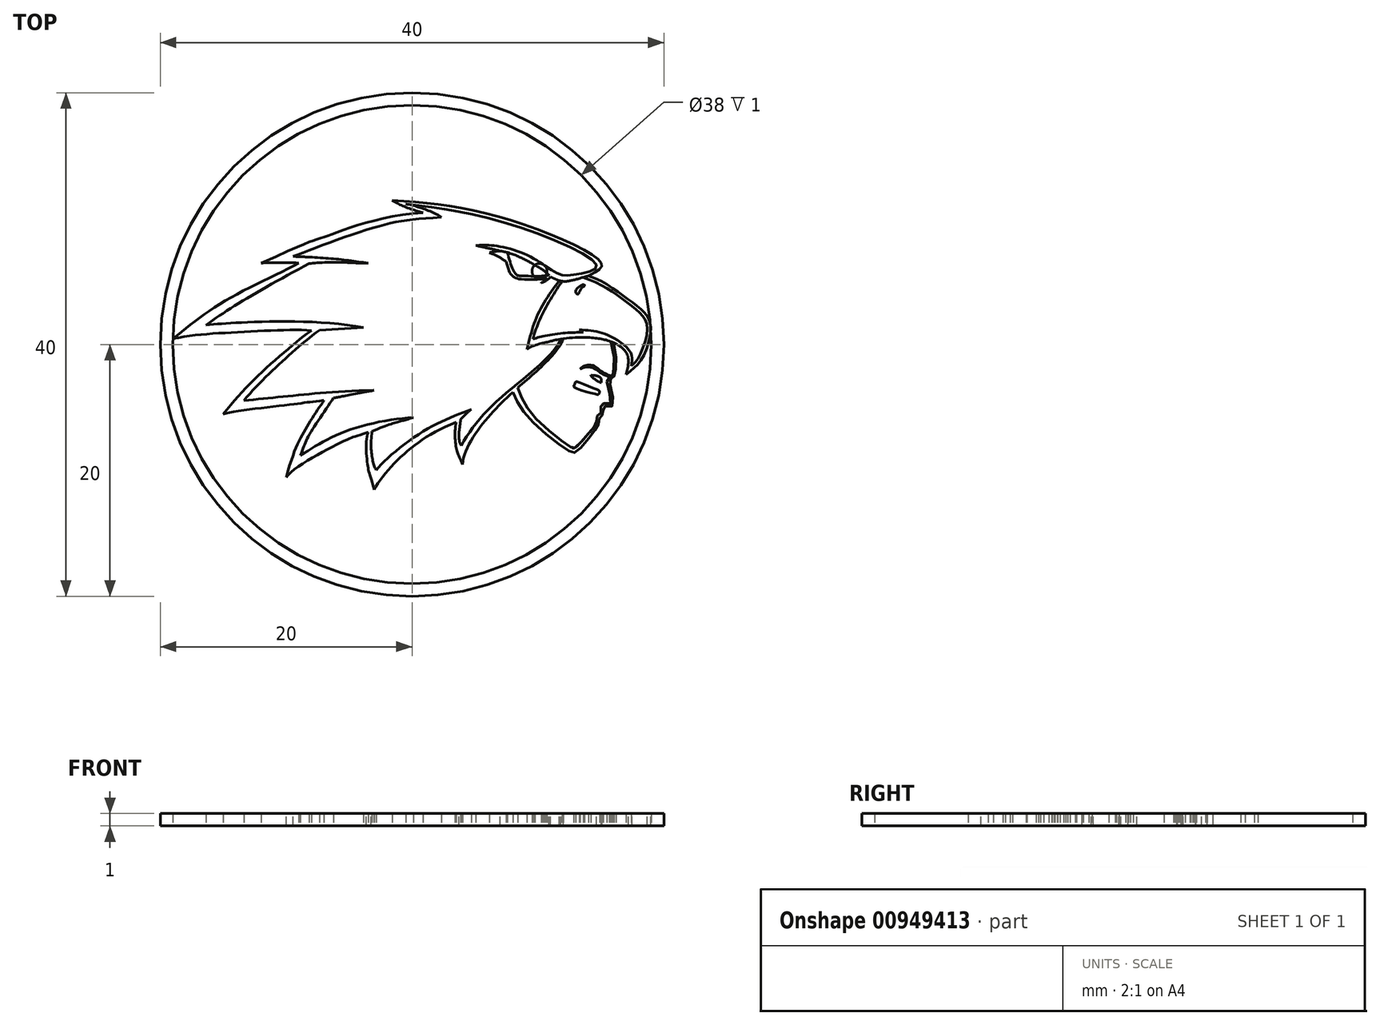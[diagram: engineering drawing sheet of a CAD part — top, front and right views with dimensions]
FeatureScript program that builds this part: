
annotation { "Feature Type Name" : "Feature", "Feature Type Description" : "" }
export const myFeature = defineFeature(function(context is Context, id is Id, definition is map)
    precondition{}
    {
        {
            var Q0;
            Q0=qCreatedBy(makeId("Top.planeOp"),FACE);
            var sketch = newSketch(context, id + "F0", { "sketchPlane" : qUnion([Q0])});
            skCircle(sketch, "E0", {"center": v(0, 0) * mm, "radius": 20 * mm});
            skCircle(sketch, "E1", {"center": v(0, 0) * mm, "radius": 19 * mm});
            skCircle(sketch, "E2", {"center": v(0, 17) * mm, "radius": 2 * mm});
            skSolve(sketch);
        }
        {
            var Q0;
            Q0=makeQuery(id+"F0.imprint","IMPRINT",FACE,{"disambiguationData":[TD([[makeQuery(id+"F0.imprint","IMPRINT",EDGE,{"derivedFrom":sQuery(id+"F0.wireOp",EDGE,"E0")}),1.0]])]});
            extrude(context, id + "F1", {"entities" : qUnion([Q0]), "depth" : 1 * mm, "offsetDistance" : 25 * mm});
        }
        {
            var Q0;
            Q0=qCreatedBy(makeId("Top.planeOp"),FACE);
            var sketch = newSketch(context, id + "F2", { "sketchPlane" : qUnion([Q0])});
            skFitSpline(sketch, "E3", {"points": [v(-1.58, 11.45) * mm, v(7.72, 9.91) * mm, v(15.05, 6.42) * mm, v(14, 5.45) * mm], "startDerivative": vector(21.52, -1.26) * mm, "endDerivative": vector(-13.3, -6.93) * mm});
            skFitSpline(sketch, "E4", {"points": [v(3.5, -6.16) * mm, v(-0.78, -8.83) * mm, v(-3, -11.55) * mm], "startDerivative": vector(-10.76, -4.46) * mm, "endDerivative": vector(-2.73, -5.76) * mm});
            skFitSpline(sketch, "E5", {"points": [v(-3, -11.55) * mm, v(-3.55, -9.5) * mm, v(-3.5, -6.96) * mm], "startDerivative": vector(-2.35, 7.78) * mm, "endDerivative": vector(1.35, 3.27) * mm});
            skFitSpline(sketch, "E6", {"points": [v(-3.5, -6.96) * mm, v(-5.27, -7.6) * mm, v(-10, -10.55) * mm], "startDerivative": vector(-9.15, -3.1) * mm, "endDerivative": vector(-2.97, -4.21) * mm});
            skFitSpline(sketch, "E7", {"points": [v(-10, -10.55) * mm, v(-8.32, -6.48) * mm, v(-7, -4.44) * mm], "startDerivative": vector(3.25, 11.93) * mm, "endDerivative": vector(2.66, 3.7) * mm});
            skFitSpline(sketch, "E8", {"points": [v(-7, -4.44) * mm, v(-9.47, -4.75) * mm, v(-15, -5.55) * mm], "startDerivative": vector(-8.24, -0.84) * mm, "endDerivative": vector(-4.12, -1.43) * mm});
            skFitSpline(sketch, "E9", {"points": [v(-15, -5.55) * mm, v(-11, -1.34) * mm, v(-8, 1.1) * mm], "startDerivative": vector(6.54, 8.64) * mm, "endDerivative": vector(3.53, 2.33) * mm});
            skFitSpline(sketch, "E10", {"points": [v(-8, 1.1) * mm, v(-13.7, 0.98) * mm, v(-19, 0.45) * mm], "startDerivative": vector(-8.4, 0.77) * mm, "endDerivative": vector(-10.04, -2.22) * mm});
            skFitSpline(sketch, "E11", {"points": [v(-19, 0.45) * mm, v(-14.13, 3.88) * mm, v(-8, 7.05) * mm], "startDerivative": vector(8.8, 7.31) * mm, "endDerivative": vector(6.6, 4.65) * mm});
            skFitSpline(sketch, "E12", {"points": [v(-12, 6.45) * mm, v(-6.88, 8.58) * mm, v(0.86, 10.45) * mm], "startDerivative": vector(30.08, 13.67) * mm, "endDerivative": vector(18.85, 0.85) * mm});
            skFitSpline(sketch, "E13", {"points": [v(0.86, 10.45) * mm, v(-0.78, 11.03) * mm, v(-1.58, 11.45) * mm], "startDerivative": vector(-2.07, 0.66) * mm, "endDerivative": vector(-0.97, 0.57) * mm});
            skFitSpline(sketch, "E14", {"points": [v(3.5, -6.16) * mm, v(3.53, -8.34) * mm, v(4, -9.55) * mm], "startDerivative": vector(-0.77, -3.97) * mm, "endDerivative": vector(1.6, -4.4) * mm});
            skFitSpline(sketch, "E15", {"points": [v(4, -9.55) * mm, v(5.91, -5.94) * mm, v(9.09, -2.83) * mm, v(12, 0.45) * mm], "startDerivative": vector(0.54, 10.48) * mm, "endDerivative": vector(2.95, 8.84) * mm});
            skFitSpline(sketch, "E16", {"points": [v(-9, 6.45) * mm, v(-10.52, 6.5) * mm, v(-12, 6.45) * mm], "startDerivative": vector(-3.14, 0.42) * mm, "endDerivative": vector(-2.86, -0.43) * mm});
            skFitSpline(sketch, "E17", {"points": [v(14, 5.45) * mm, v(16.43, 4.12) * mm, v(18.07, 2.88) * mm, v(18.94, 1.52) * mm, v(18.18, -1.26) * mm, v(17, -2.4) * mm], "startDerivative": vector(12.4, -3.48) * mm, "endDerivative": vector(-8.18, -8.07) * mm});
            skFitSpline(sketch, "E18", {"points": [v(17, -2.4) * mm, v(17.07, -0.75) * mm, v(15.73, 0.25) * mm, v(14.63, 0.5) * mm, v(12, 0.45) * mm], "startDerivative": vector(1.76, 6.26) * mm, "endDerivative": vector(-11.27, -1.86) * mm});
            skFitSpline(sketch, "E19", {"points": [v(11, 5.38) * mm, v(9.78, 6.3) * mm, v(7, 7.43) * mm], "startDerivative": vector(-2.8, 3.17) * mm, "endDerivative": vector(-5.7, 0.83) * mm});
            skFitSpline(sketch, "E20", {"points": [v(7, 7.43) * mm, v(7.74, 5.78) * mm, v(8, 5.43) * mm, v(8.44, 5.22) * mm, v(10.45, 5.2) * mm, v(10.9, 5.29) * mm, v(11, 5.38) * mm], "startDerivative": vector(6.03, -7.57) * mm, "endDerivative": vector(2.14, 2.82) * mm});
            skCircle(sketch, "E21", {"center": v(10.12, 5.84) * mm, "radius": 0.6 * mm});
            skFitSpline(sketch, "E22", {"points": [v(8, -3.8) * mm, v(9.3, -5.87) * mm, v(12.45, -8.44) * mm, v(13, -8.55) * mm, v(14.33, -7.05) * mm, v(14.82, -6.23) * mm, v(14.93, -5.76) * mm, v(15.19, -5.5) * mm, v(15.2, -4.92) * mm, v(15.93, -4.86) * mm, v(15.7, -2.86) * mm, v(15.92, -2.64) * mm, v(16.1, -2.38) * mm, v(16, 0.14) * mm], "startDerivative": vector(7.5, -17.46) * mm, "endDerivative": vector(-8.07, 26.27) * mm});
            skFitSpline(sketch, "E23", {"points": [v(15.02, -3.03) * mm, v(14.56, -2.8) * mm, v(14.2, -2.44) * mm], "startDerivative": vector(-1.12, 0.33) * mm, "endDerivative": vector(-0.33, 0.79) * mm});
            skFitSpline(sketch, "E24", {"points": [v(14.2, -2.44) * mm, v(14.57, -2.47) * mm, v(14.94, -2.61) * mm, v(15.04, -2.8) * mm, v(15.02, -3.03) * mm], "startDerivative": vector(1.37, -0.38) * mm, "endDerivative": vector(-0.15, -0.97) * mm});
            skFitSpline(sketch, "E25", {"points": [v(15.68, -2.55) * mm, v(15.48, -2.5) * mm, v(14.93, -2.22) * mm, v(14.67, -2.02) * mm, v(14.03, -1.79) * mm, v(13.34, -1.95) * mm], "startDerivative": vector(-2.24, 0.34) * mm, "endDerivative": vector(-2.61, -1.2) * mm});
            skFitSpline(sketch, "E26", {"points": [v(13.34, -1.95) * mm, v(13.86, -1.65) * mm, v(14.3, -1.65) * mm, v(14.57, -1.77) * mm, v(15.07, -2.15) * mm, v(15.55, -2.4) * mm, v(15.89, -2.49) * mm], "startDerivative": vector(2.26, 2.4) * mm, "endDerivative": vector(2.1, 0.6) * mm});
            skFitSpline(sketch, "E27", {"points": [v(15.68, -2.55) * mm, v(15.8, -2.54) * mm, v(15.89, -2.49) * mm], "startDerivative": vector(0.25, -0.06) * mm, "endDerivative": vector(0.25, 0.3) * mm});
            skFitSpline(sketch, "E28", {"points": [v(14.52, -3.93) * mm, v(12.97, -3.46) * mm, v(12.85, -3.33) * mm, v(12.9, -3.2) * mm, v(12.98, -3) * mm, v(13.07, -2.94) * mm, v(13.22, -3) * mm, v(14.68, -3.57) * mm, v(14.86, -3.66) * mm, v(14.9, -3.76) * mm, v(14.84, -3.93) * mm, v(14.78, -3.97) * mm, v(14.52, -3.93) * mm]});
            skFitSpline(sketch, "E29", {"points": [v(12, 0.45) * mm, v(10.73, 0.2) * mm, v(9.12, -0.4) * mm], "startDerivative": vector(-4.79, -0.65) * mm, "endDerivative": vector(-1.75, -1.76) * mm});
            skFitSpline(sketch, "E30", {"points": [v(9.12, -0.4) * mm, v(10.04, 2.5) * mm, v(11.7, 5.07) * mm], "startDerivative": vector(1.47, 5.98) * mm, "endDerivative": vector(3.7, 4.95) * mm});
            skFitSpline(sketch, "E31", {"points": [v(14, 5.45) * mm, v(12.41, 5.04) * mm, v(11.7, 5.07) * mm, v(11, 5.38) * mm], "startDerivative": vector(-4.1, -1.19) * mm, "endDerivative": vector(-2.43, 1.23) * mm});
            skFitSpline(sketch, "E32", {"points": [v(7, 7.43) * mm, v(5.97, 7.67) * mm, v(5.07, 7.87) * mm], "startDerivative": vector(-2.03, 0.53) * mm, "endDerivative": vector(-1.84, 0.4) * mm});
            skFitSpline(sketch, "E33", {"points": [v(5.07, 7.87) * mm, v(6.4, 7.87) * mm, v(9.35, 7) * mm, v(11.6, 5.62) * mm, v(12.86, 5.54) * mm, v(14.66, 6.18) * mm, v(7.76, 9.56) * mm, v(-0.49, 11.17) * mm], "startDerivative": vector(13.05, 0.9) * mm, "endDerivative": vector(-32.62, 3.92) * mm});
            skFitSpline(sketch, "E34", {"points": [v(-0.49, 11.17) * mm, v(0.93, 10.77) * mm, v(2.33, 10.11) * mm], "startDerivative": vector(2.94, -0.6) * mm, "endDerivative": vector(1.78, -1.4) * mm});
            skFitSpline(sketch, "E35", {"points": [v(2.33, 10.11) * mm, v(-3.07, 9.27) * mm, v(-9.44, 7) * mm], "startDerivative": vector(-15.85, -1) * mm, "endDerivative": vector(-7.4, -3.02) * mm});
            skFitSpline(sketch, "E36", {"points": [v(-9.44, 7) * mm, v(-6.18, 6.8) * mm, v(-3.48, 6.45) * mm], "startDerivative": vector(6.38, -0.27) * mm, "endDerivative": vector(5.53, -0.87) * mm});
            skFitSpline(sketch, "E37", {"points": [v(-3.48, 6.45) * mm, v(-6.21, 6.54) * mm, v(-8.18, 6.43) * mm], "startDerivative": vector(-6.33, 0.08) * mm, "endDerivative": vector(-3.05, -0.33) * mm});
            skFitSpline(sketch, "E38", {"points": [v(-8.18, 6.43) * mm, v(-13.5, 3.44) * mm, v(-16.37, 1.55) * mm], "startDerivative": vector(-9.86, -5.27) * mm, "endDerivative": vector(-6.1, -4.23) * mm});
            skFitSpline(sketch, "E39", {"points": [v(-16.37, 1.55) * mm, v(-13.5, 1.75) * mm, v(-3.85, 1.35) * mm], "startDerivative": vector(6.8, 0.6) * mm, "endDerivative": vector(14.41, -2.83) * mm});
            skFitSpline(sketch, "E40", {"points": [v(-3.85, 1.35) * mm, v(-7.35, 1.14) * mm], "startDerivative": vector(-3.5, -0.2) * mm, "endDerivative": vector(-3.5, -0.2) * mm});
            skFitSpline(sketch, "E41", {"points": [v(-7.35, 1.14) * mm, v(-10.41, -1.43) * mm, v(-13.36, -4.46) * mm], "startDerivative": vector(-6.68, -4.88) * mm, "endDerivative": vector(-5.36, -6.32) * mm});
            skFitSpline(sketch, "E42", {"points": [v(-13.36, -4.46) * mm, v(-9.36, -4.06) * mm, v(-3.02, -3.64) * mm], "startDerivative": vector(8.78, 0.94) * mm, "endDerivative": vector(14.42, 0.16) * mm});
            skFitSpline(sketch, "E43", {"points": [v(-3.02, -3.64) * mm, v(-5.54, -4.12) * mm, v(-6.24, -4.25) * mm], "startDerivative": vector(-4.48, -0.91) * mm, "endDerivative": vector(-1.64, -0.24) * mm});
            skFitSpline(sketch, "E44", {"points": [v(-6.24, -4.25) * mm, v(-8.21, -7.25) * mm, v(-8.87, -8.8) * mm], "startDerivative": vector(-3.02, -4.33) * mm, "endDerivative": vector(-1.83, -4.96) * mm});
            skFitSpline(sketch, "E45", {"points": [v(-8.87, -8.8) * mm, v(-5.6, -7.02) * mm, v(0.1, -5.81) * mm], "startDerivative": vector(6.74, 4.12) * mm, "endDerivative": vector(9.55, 0.33) * mm});
            skFitSpline(sketch, "E46", {"points": [v(0.1, -5.81) * mm, v(-1.02, -6.13) * mm, v(-3.18, -6.9) * mm], "startDerivative": vector(-4.07, -1.11) * mm, "endDerivative": vector(-5.58, -2.4) * mm});
            skFitSpline(sketch, "E47", {"points": [v(-3.18, -6.9) * mm, v(-3.14, -9.14) * mm, v(-2.84, -9.97) * mm], "startDerivative": vector(-0.7, -4.41) * mm, "endDerivative": vector(1.32, -1.52) * mm});
            skFitSpline(sketch, "E48", {"points": [v(-2.84, -9.97) * mm, v(0.78, -6.97) * mm, v(4.7, -5.14) * mm], "startDerivative": vector(3.54, 4.6) * mm, "endDerivative": vector(7.5, 2.99) * mm});
            skFitSpline(sketch, "E49", {"points": [v(4.7, -5.14) * mm, v(3.85, -5.96) * mm], "startDerivative": vector(-1.54, -1.24) * mm, "endDerivative": vector(-0.85, -0.81) * mm});
            skFitSpline(sketch, "E50", {"points": [v(3.85, -5.96) * mm, v(3.74, -7.58) * mm, v(3.91, -8.04) * mm], "startDerivative": vector(-0.38, -2.91) * mm, "endDerivative": vector(0.59, -1.08) * mm});
            skFitSpline(sketch, "E51", {"points": [v(3.91, -8.04) * mm, v(5.56, -5.69) * mm, v(8.66, -2.88) * mm, v(11.8, 0.43) * mm], "startDerivative": vector(4.66, 8.5) * mm, "endDerivative": vector(3.92, 9.27) * mm});
            skFitSpline(sketch, "E52", {"points": [v(11.8, 0.43) * mm, v(12, 0.45) * mm], "startDerivative": vector(0.2, 0.03) * mm, "endDerivative": vector(0.2, 0.03) * mm});
            skFitSpline(sketch, "E53", {"points": [v(11.92, 5.03) * mm, v(10.4, 2.5) * mm, v(9.6, 0.43) * mm], "startDerivative": vector(-3.21, -4.76) * mm, "endDerivative": vector(-1.06, -4.44) * mm});
            skFitSpline(sketch, "E54", {"points": [v(9.6, 0.43) * mm, v(10.45, 0.67) * mm, v(12.21, 0.92) * mm, v(13.6, 0.96) * mm], "startDerivative": vector(2.74, 0.91) * mm, "endDerivative": vector(3.8, 0) * mm});
            skFitSpline(sketch, "E55", {"points": [v(13.6, 0.96) * mm, v(13.29, 1.17) * mm], "startDerivative": vector(-0.45, 0.21) * mm, "endDerivative": vector(-0.45, 0.21) * mm});
            skFitSpline(sketch, "E56", {"points": [v(13.29, 1.17) * mm, v(14.52, 1.05) * mm, v(15.83, 0.62) * mm, v(17.37, -0.67) * mm, v(17.4, -1.7) * mm], "startDerivative": vector(5.3, -0.38) * mm, "endDerivative": vector(-0.98, -4.8) * mm});
            skFitSpline(sketch, "E57", {"points": [v(17.4, -1.7) * mm, v(17.94, -1.12) * mm, v(18.7, 1.36) * mm, v(18, 2.6) * mm, v(16.13, 4.03) * mm, v(13.6, 5.34) * mm], "startDerivative": vector(3.88, 3.06) * mm, "endDerivative": vector(-12.32, 4.18) * mm});
            skFitSpline(sketch, "E58", {"points": [v(7.57, 7.3) * mm, v(8.08, 5.8) * mm, v(8.4, 5.5) * mm, v(8.78, 5.45) * mm, v(10.88, 5.51) * mm], "startDerivative": vector(1.53, -5.22) * mm, "endDerivative": vector(2.76, 1.11) * mm});
            skFitSpline(sketch, "E59", {"points": [v(7.48, 6.59) * mm, v(6.84, 6.98) * mm, v(6.14, 7.3) * mm], "startDerivative": vector(-1.21, 0.84) * mm, "endDerivative": vector(-1.25, 0.39) * mm});
            skFitSpline(sketch, "E60", {"points": [v(7, 7.43) * mm, v(6.54, 7.38) * mm, v(6.14, 7.3) * mm], "startDerivative": vector(-0.92, 0.03) * mm, "endDerivative": vector(-1.04, -0.3) * mm});
            skFitSpline(sketch, "E61", {"points": [v(11, 5.38) * mm, v(10.6, 5.04) * mm, v(10.25, 4.9) * mm], "startDerivative": vector(-0.74, -0.71) * mm, "endDerivative": vector(-0.76, -0.25) * mm});
            skFitSpline(sketch, "E62", {"points": [v(10.25, 4.9) * mm, v(10.65, 5.17) * mm, v(10.88, 5.51) * mm], "startDerivative": vector(0.83, 0.5) * mm, "endDerivative": vector(0.41, 0.76) * mm});
            skFitSpline(sketch, "E63", {"points": [v(13.68, 4.76) * mm, v(13.18, 4.53) * mm, v(13.02, 4.13) * mm, v(13.16, 4) * mm, v(13.46, 4.47) * mm, v(13.69, 4.66) * mm, v(13.68, 4.76) * mm]});
            skFitSpline(sketch, "E64", {"points": [v(15.8, 0.23) * mm, v(15.96, -2.32) * mm, v(15.87, -2.55) * mm, v(15.5, -2.74) * mm, v(15.75, -4.67) * mm, v(15.05, -4.7) * mm, v(15, -5.4) * mm, v(14.74, -5.63) * mm, v(14.63, -6.18) * mm, v(14.19, -6.88) * mm, v(12.96, -8.19) * mm, v(12.6, -8.15) * mm, v(9.58, -5.6) * mm, v(8.38, -3.45) * mm], "startDerivative": vector(10.2, -30.63) * mm, "endDerivative": vector(-7.66, 17.6) * mm});
            skFitSpline(sketch, "E65", {"points": [v(10.7, 5.68) * mm, v(10.67, 6.08) * mm, v(10.45, 6.34) * mm], "startDerivative": vector(0.04, 0.82) * mm, "endDerivative": vector(-0.55, 0.49) * mm});
            skFitSpline(sketch, "E66", {"points": [v(3.5, -6.16) * mm, v(3.85, -5.96) * mm], "startDerivative": vector(0.35, 0.2) * mm, "endDerivative": vector(0.35, 0.2) * mm});
            skFitSpline(sketch, "E67", {"points": [v(-2.84, -9.97) * mm, v(-3, -11.55) * mm], "startDerivative": vector(-0.16, -1.59) * mm, "endDerivative": vector(-0.16, -1.59) * mm});
            skFitSpline(sketch, "E68", {"points": [v(-3.18, -6.9) * mm, v(-3.5, -6.96) * mm], "startDerivative": vector(-0.31, -0.06) * mm, "endDerivative": vector(-0.31, -0.06) * mm});
            skFitSpline(sketch, "E69", {"points": [v(-8.87, -8.8) * mm, v(-10, -10.55) * mm], "startDerivative": vector(-1.13, -1.75) * mm, "endDerivative": vector(-1.13, -1.75) * mm});
            skFitSpline(sketch, "E70", {"points": [v(-7, -4.44) * mm, v(-6.24, -4.25) * mm], "startDerivative": vector(0.76, 0.19) * mm, "endDerivative": vector(0.76, 0.19) * mm});
            skFitSpline(sketch, "E71", {"points": [v(-13.36, -4.46) * mm, v(-15, -5.55) * mm], "startDerivative": vector(-1.63, -1.1) * mm, "endDerivative": vector(-1.63, -1.1) * mm});
            skFitSpline(sketch, "E72", {"points": [v(-8, 1.1) * mm, v(-7.35, 1.14) * mm], "startDerivative": vector(0.65, 0.03) * mm, "endDerivative": vector(0.65, 0.03) * mm});
            skFitSpline(sketch, "E73", {"points": [v(-16.37, 1.55) * mm, v(-19, 0.45) * mm], "startDerivative": vector(-2.63, -1.1) * mm, "endDerivative": vector(-2.63, -1.1) * mm});
            skFitSpline(sketch, "E74", {"points": [v(-9, 6.45) * mm, v(-8.18, 6.43) * mm], "startDerivative": vector(0.82, -0.01) * mm, "endDerivative": vector(0.82, -0.01) * mm});
            skFitSpline(sketch, "E75", {"points": [v(-9.44, 7) * mm, v(-12, 6.45) * mm], "startDerivative": vector(-2.56, -0.56) * mm, "endDerivative": vector(-2.56, -0.56) * mm});
            skFitSpline(sketch, "E76", {"points": [v(0.86, 10.45) * mm, v(2.33, 10.11) * mm], "startDerivative": vector(1.48, -0.33) * mm, "endDerivative": vector(1.48, -0.33) * mm});
            skFitSpline(sketch, "E77", {"points": [v(-0.49, 11.17) * mm, v(-1.58, 11.45) * mm], "startDerivative": vector(-1.1, 0.27) * mm, "endDerivative": vector(-1.1, 0.27) * mm});
            skFitSpline(sketch, "E78", {"points": [v(13.6, 5.34) * mm, v(14, 5.45) * mm], "startDerivative": vector(0.4, 0.12) * mm, "endDerivative": vector(0.4, 0.12) * mm});
            skFitSpline(sketch, "E79", {"points": [v(7, 7.43) * mm, v(7.57, 7.3) * mm], "startDerivative": vector(0.57, -0.12) * mm, "endDerivative": vector(0.57, -0.12) * mm});
            skSolve(sketch);
        }
        {
            var Q0;
            {var subQ2=sQuery(id+"F2.wireOp",EDGE,"E59");Q0=makeQuery(id+"F2.imprint","IMPRINT",FACE,{"disambiguationData":[TD([[makeQuery(id+"F2.imprint","IMPRINT",EDGE,{"derivedFrom":subQ2}),-1.0]])]});}
            var Q1;
            Q1=makeQuery(id+"F2.imprint","IMPRINT",FACE,{"disambiguationData":[TD([[makeQuery(id+"F2.imprint","IMPRINT",EDGE,{"derivedFrom":sQuery(id+"F2.wireOp",EDGE,"E63")}),1.0]])]});
            var Q2;
            {var subQ0=sQuery(id+"F2.wireOp",EDGE,"E32");Q2=makeQuery(id+"F2.imprint","IMPRINT",FACE,{"disambiguationData":[TD([[makeQuery(id+"F2.imprint","IMPRINT",EDGE,{"derivedFrom":subQ0}),-1.0]])]});}
            var Q3;
            {var subQ0=sQuery(id+"F2.wireOp",EDGE,"E79");Q3=makeQuery(id+"F2.imprint","IMPRINT",FACE,{"disambiguationData":[TD([[makeQuery(id+"F2.imprint","IMPRINT",EDGE,{"derivedFrom":subQ0}),-1.0]])]});}
            var Q4;
            Q4=makeQuery(id+"F2.imprint","IMPRINT",FACE,{"disambiguationData":[TD([[makeQuery(id+"F2.imprint","IMPRINT",EDGE,{"derivedFrom":sQuery(id+"F2.wireOp",EDGE,"E3")}),-1.0]])]});
            var Q5;
            {var subQ0=sQuery(id+"F2.wireOp",EDGE,"E62");var subQ1=sQuery(id+"F2.wireOp",EDGE,"E20");var subQ2=makeQuery(id+"F2.imprint","INTERSECT",VERTEX,{"derivedFrom":[subQ1,subQ0]});Q5=makeQuery(id+"F2.imprint","IMPRINT",FACE,{"disambiguationData":[TD([[makeQuery(id+"F2.imprint","IMPRINT",EDGE,{"disambiguationData":[TD([[subQ2,-1.0]])],"derivedFrom":subQ1}),-1.0]])]});}
            var Q6;
            {var subQ1=sQuery(id+"F2.wireOp",EDGE,"E20");var subQ4=sQuery(id+"F2.wireOp",EDGE,"E62");var subQ6=makeQuery(id+"F2.imprint","INTERSECT",VERTEX,{"derivedFrom":[subQ1,subQ4]});Q6=makeQuery(id+"F2.imprint","IMPRINT",FACE,{"disambiguationData":[TD([[makeQuery(id+"F2.imprint","IMPRINT",EDGE,{"disambiguationData":[TD([[subQ6,-1.0]])],"derivedFrom":subQ1}),1.0]])]});}
            var Q7;
            {var subQ0=sQuery(id+"F2.wireOp",EDGE,"E21");var subQ1=sQuery(id+"F2.wireOp",EDGE,"E19");var subQ3=makeQuery(id+"F2.imprint","INTERSECT",VERTEX,{"derivedFrom":[subQ1,subQ0]});Q7=makeQuery(id+"F2.imprint","IMPRINT",FACE,{"disambiguationData":[TD([[makeQuery(id+"F2.imprint","IMPRINT",EDGE,{"disambiguationData":[TD([[subQ3,-1.0]])],"derivedFrom":subQ0}),1.0]])]});}
            var Q8;
            {var subQ4=sQuery(id+"F2.wireOp",EDGE,"E14");Q8=makeQuery(id+"F2.imprint","IMPRINT",FACE,{"disambiguationData":[TD([[makeQuery(id+"F2.imprint","IMPRINT",EDGE,{"derivedFrom":subQ4}),1.0]])]});}
            var Q9;
            {var subQ0=sQuery(id+"F2.wireOp",EDGE,"E22");Q9=makeQuery(id+"F2.imprint","IMPRINT",FACE,{"disambiguationData":[TD([[makeQuery(id+"F2.imprint","IMPRINT",EDGE,{"derivedFrom":subQ0}),1.0]])]});}
            var Q10;
            Q10=makeQuery(id+"F2.imprint","IMPRINT",FACE,{"disambiguationData":[TD([[makeQuery(id+"F2.imprint","IMPRINT",EDGE,{"derivedFrom":sQuery(id+"F2.wireOp",EDGE,"E23")}),-1.0]])]});
            var Q11;
            Q11=makeQuery(id+"F2.imprint","IMPRINT",FACE,{"disambiguationData":[TD([[makeQuery(id+"F2.imprint","IMPRINT",EDGE,{"derivedFrom":sQuery(id+"F2.wireOp",EDGE,"E28")}),-1.0]])]});
            var Q12;
            Q12=makeQuery(id+"F2.imprint","IMPRINT",FACE,{"disambiguationData":[TD([[makeQuery(id+"F2.imprint","IMPRINT",EDGE,{"derivedFrom":sQuery(id+"F2.wireOp",EDGE,"E25")}),-1.0]])]});
            var Q13;
            Q13=makeQuery(id+"F2.imprint","IMPRINT",FACE,{"disambiguationData":[TD([[makeQuery(id+"F2.imprint","IMPRINT",EDGE,{"derivedFrom":sQuery(id+"F2.wireOp",EDGE,"E4")}),-1.0]])]});
            var Q14;
            Q14=makeQuery(id+"F2.imprint","IMPRINT",FACE,{"disambiguationData":[TD([[makeQuery(id+"F2.imprint","IMPRINT",EDGE,{"derivedFrom":sQuery(id+"F2.wireOp",EDGE,"E5")}),-1.0]])]});
            var Q15;
            Q15=makeQuery(id+"F2.imprint","IMPRINT",FACE,{"disambiguationData":[TD([[makeQuery(id+"F2.imprint","IMPRINT",EDGE,{"derivedFrom":sQuery(id+"F2.wireOp",EDGE,"E6")}),-1.0]])]});
            var Q16;
            Q16=makeQuery(id+"F2.imprint","IMPRINT",FACE,{"disambiguationData":[TD([[makeQuery(id+"F2.imprint","IMPRINT",EDGE,{"derivedFrom":sQuery(id+"F2.wireOp",EDGE,"E7")}),-1.0]])]});
            var Q17;
            Q17=makeQuery(id+"F2.imprint","IMPRINT",FACE,{"disambiguationData":[TD([[makeQuery(id+"F2.imprint","IMPRINT",EDGE,{"derivedFrom":sQuery(id+"F2.wireOp",EDGE,"E8")}),-1.0]])]});
            var Q18;
            Q18=makeQuery(id+"F2.imprint","IMPRINT",FACE,{"disambiguationData":[TD([[makeQuery(id+"F2.imprint","IMPRINT",EDGE,{"derivedFrom":sQuery(id+"F2.wireOp",EDGE,"E9")}),-1.0]])]});
            var Q19;
            Q19=makeQuery(id+"F2.imprint","IMPRINT",FACE,{"disambiguationData":[TD([[makeQuery(id+"F2.imprint","IMPRINT",EDGE,{"derivedFrom":sQuery(id+"F2.wireOp",EDGE,"E10")}),-1.0]])]});
            var Q20;
            Q20=makeQuery(id+"F2.imprint","IMPRINT",FACE,{"disambiguationData":[TD([[makeQuery(id+"F2.imprint","IMPRINT",EDGE,{"derivedFrom":sQuery(id+"F2.wireOp",EDGE,"E11")}),-1.0]])]});
            var Q21;
            Q21=makeQuery(id+"F2.imprint","IMPRINT",FACE,{"disambiguationData":[TD([[makeQuery(id+"F2.imprint","IMPRINT",EDGE,{"derivedFrom":sQuery(id+"F2.wireOp",EDGE,"E12")}),-1.0]])]});
            var Q22;
            Q22=makeQuery(id+"F2.imprint","IMPRINT",FACE,{"disambiguationData":[TD([[makeQuery(id+"F2.imprint","IMPRINT",EDGE,{"derivedFrom":sQuery(id+"F2.wireOp",EDGE,"E13")}),-1.0]])]});
            var Q23;
            Q23=makeQuery(id+"F2.imprint","IMPRINT",FACE,{"disambiguationData":[TD([[makeQuery(id+"F2.imprint","IMPRINT",EDGE,{"derivedFrom":sQuery(id+"F2.wireOp",EDGE,"E16")}),-1.0]])]});
            extrude(context, id + "F3", {"entities" : qUnion([Q0, Q1, Q2, Q3, Q4, Q5, Q6, Q7, Q8, Q9, Q10, Q11, Q12, Q13, Q14, Q15, Q16, Q17, Q18, Q19, Q20, Q21, Q22, Q23]), "depth" : 1 * mm, "offsetDistance" : 25 * mm});
        }
        {
            var Q0;
            {var subQ1=sQuery(id+"F2.wireOp",EDGE,"E21");var subQ3=sQuery(id+"F2.wireOp",EDGE,"E65");var subQ8=makeQuery(id+"F2.imprint","INTERSECT",VERTEX,{"disambiguationData":[OD(1.0)],"derivedFrom":[subQ1,subQ3]});Q0=makeQuery(id+"F2.imprint","IMPRINT",FACE,{"disambiguationData":[TD([[makeQuery(id+"F2.imprint","IMPRINT",EDGE,{"disambiguationData":[TD([[subQ8,1.0]])],"derivedFrom":subQ1}),1.0]])]});}
            var Q1;
            {var subQ0=sQuery(id+"F2.wireOp",EDGE,"E58");var subQ1=sQuery(id+"F2.wireOp",EDGE,"E21");var subQ2=makeQuery(id+"F2.imprint","INTERSECT",VERTEX,{"disambiguationData":[OD(0.0)],"derivedFrom":[subQ1,subQ0]});Q1=makeQuery(id+"F2.imprint","IMPRINT",FACE,{"disambiguationData":[TD([[makeQuery(id+"F2.imprint","IMPRINT",EDGE,{"disambiguationData":[TD([[subQ2,-1.0]])],"derivedFrom":subQ1}),1.0]])]});}
            var Q2;
            {var subQ3=sQuery(id+"F2.wireOp",EDGE,"E17");Q2=makeQuery(id+"F2.imprint","IMPRINT",FACE,{"disambiguationData":[TD([[makeQuery(id+"F2.imprint","IMPRINT",EDGE,{"derivedFrom":subQ3}),-1.0]])]});}
            extrude(context, id + "F4", {"entities" : qUnion([Q0, Q1, Q2]), "depth" : 1 * mm, "offsetDistance" : 25 * mm});
        }
        {
            var Q0;
            Q0=makeQuery(id+"F0.imprint","IMPRINT",FACE,{"disambiguationData":[TD([[makeQuery(id+"F0.imprint","IMPRINT",EDGE,{"derivedFrom":sQuery(id+"F0.wireOp",EDGE,"E2")}),1.0]])]});
            extrude(context, id + "F5", {"entities" : qUnion([Q0]), "operationType" : NewBodyOperationType.REMOVE, "oppositeDirection" : true, "depth" : 1 * mm, "offsetDistance" : 25 * mm});
        }
    });
